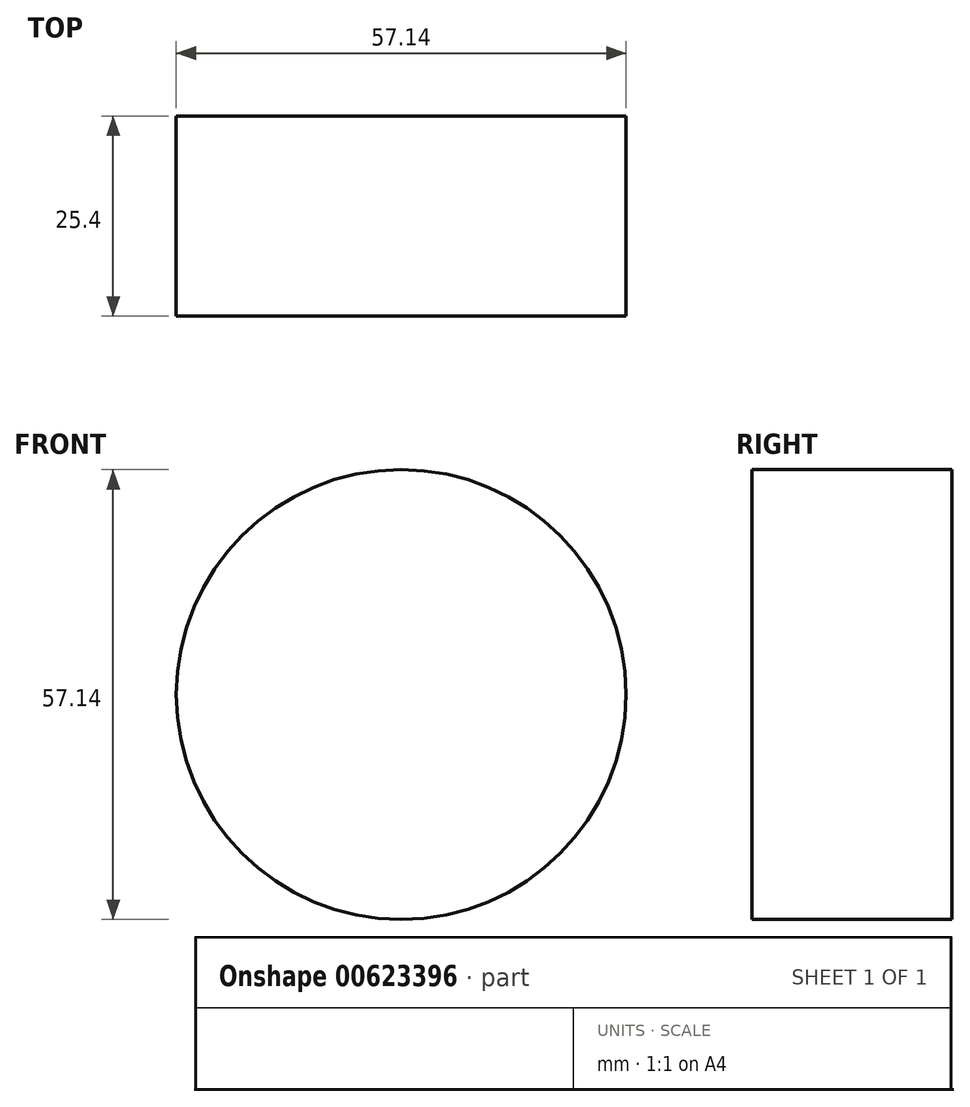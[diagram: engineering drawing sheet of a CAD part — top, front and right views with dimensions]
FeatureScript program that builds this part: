
annotation { "Feature Type Name" : "Feature", "Feature Type Description" : "" }
export const myFeature = defineFeature(function(context is Context, id is Id, definition is map)
    precondition{}
    {
        {
            var Q0;
            Q0=qCreatedBy(makeId("Front.planeOp"),FACE);
            var sketch = newSketch(context, id + "F0", { "sketchPlane" : qUnion([Q0])});
            skCircle(sketch, "E0", {"center": v(0, 0) * mm, "radius": 28.57 * mm});
            skSolve(sketch);
        }
        {
            var Q0;
            Q0=makeQuery(id+"F0.imprint","IMPRINT",FACE,{"disambiguationData":[TD([[makeQuery(id+"F0.imprint","IMPRINT",EDGE,{"derivedFrom":sQuery(id+"F0.wireOp",EDGE,"E0")}),1.0]])]});
            extrude(context, id + "F1", {"entities" : qUnion([Q0]), "depth" : 25.4 * mm, "offsetDistance" : 25.4 * mm});
        }
    });
